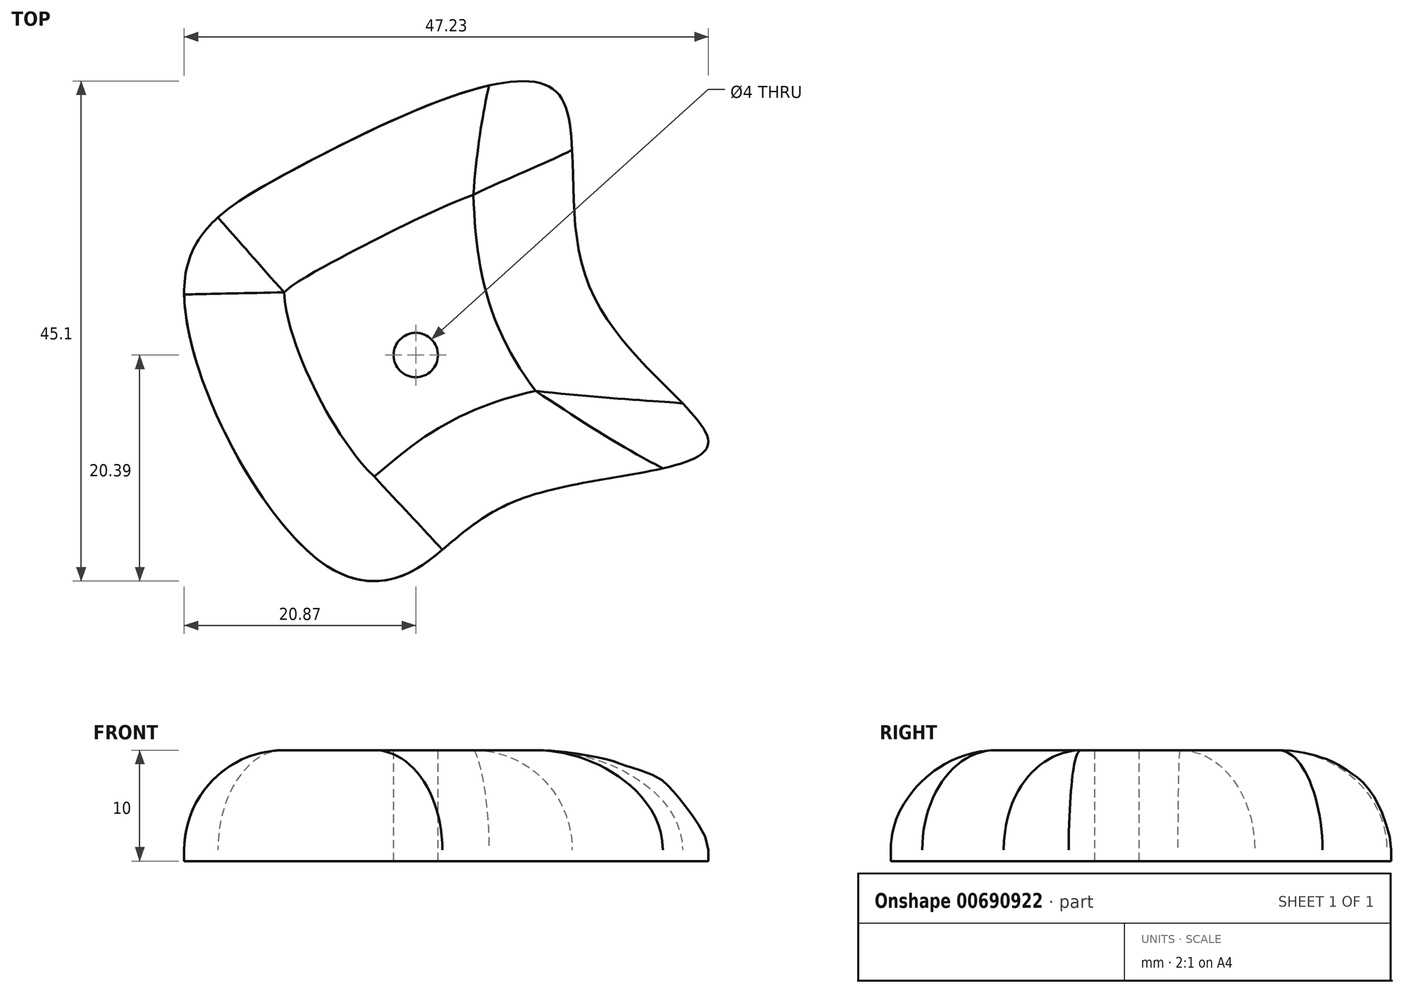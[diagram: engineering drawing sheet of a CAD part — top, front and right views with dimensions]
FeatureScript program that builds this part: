
annotation { "Feature Type Name" : "Feature", "Feature Type Description" : "" }
export const myFeature = defineFeature(function(context is Context, id is Id, definition is map)
    precondition{}
    {
        {
            var Q0;
            Q0=qCreatedBy(makeId("Top.planeOp"),FACE);
            var sketch = newSketch(context, id + "F0", { "sketchPlane" : qUnion([Q0])});
            skFitSpline(sketch, "E0", {"points": [v(9.68, -12.9) * mm, v(26.3, -8.21) * mm, v(15.75, 5.92) * mm, v(12.37, 24) * mm, v(-10.73, 16.87) * mm, v(-20.87, 5.93) * mm, v(-8.63, -18.6) * mm, v(0, -19.31) * mm, v(9.68, -12.9) * mm]});
            skSolve(sketch);
        }
        {
            var Q0;
            Q0 = qSketchRegion(id + "F0", true);
            extrude(context, id + "F1", {"entities" : qUnion([Q0]), "depth" : 10 * mm, "offsetDistance" : 25 * mm});
        }
        {
            var Q0;
            Q0=makeQuery(id+"F1.opExtrude","CAP_EDGE",EDGE,{"disambiguationData":[OSD([sQuery(id+"F0.wireOp",EDGE,"E0")])],"isStart":false});
            fillet(context, id + "F2", {"entities" : qUnion([Q0]), "radius" : 9 * mm, "tangentPropagation" : true, "allowEdgeOverflow" : false});
        }
        {
            var Q0;
            Q0=makeQuery(id+"F1.opExtrude","CAP_FACE",FACE,{"disambiguationData":[OSD([sQuery(id+"F0.wireOp",EDGE,"E0")])],"isStart":false});
            var sketch = newSketch(context, id + "F3", { "sketchPlane" : qUnion([Q0])});
            skCircle(sketch, "E1", {"center": v(0, 0) * mm, "radius": 2 * mm});
            skSolve(sketch);
        }
        {
            var Q0;
            Q0 = qSketchRegion(id + "F3", true);
            extrude(context, id + "F4", {"entities" : qUnion([Q0]), "operationType" : NewBodyOperationType.REMOVE, "oppositeDirection" : true, "depth" : 25 * mm, "offsetDistance" : 25 * mm});
        }
    });
